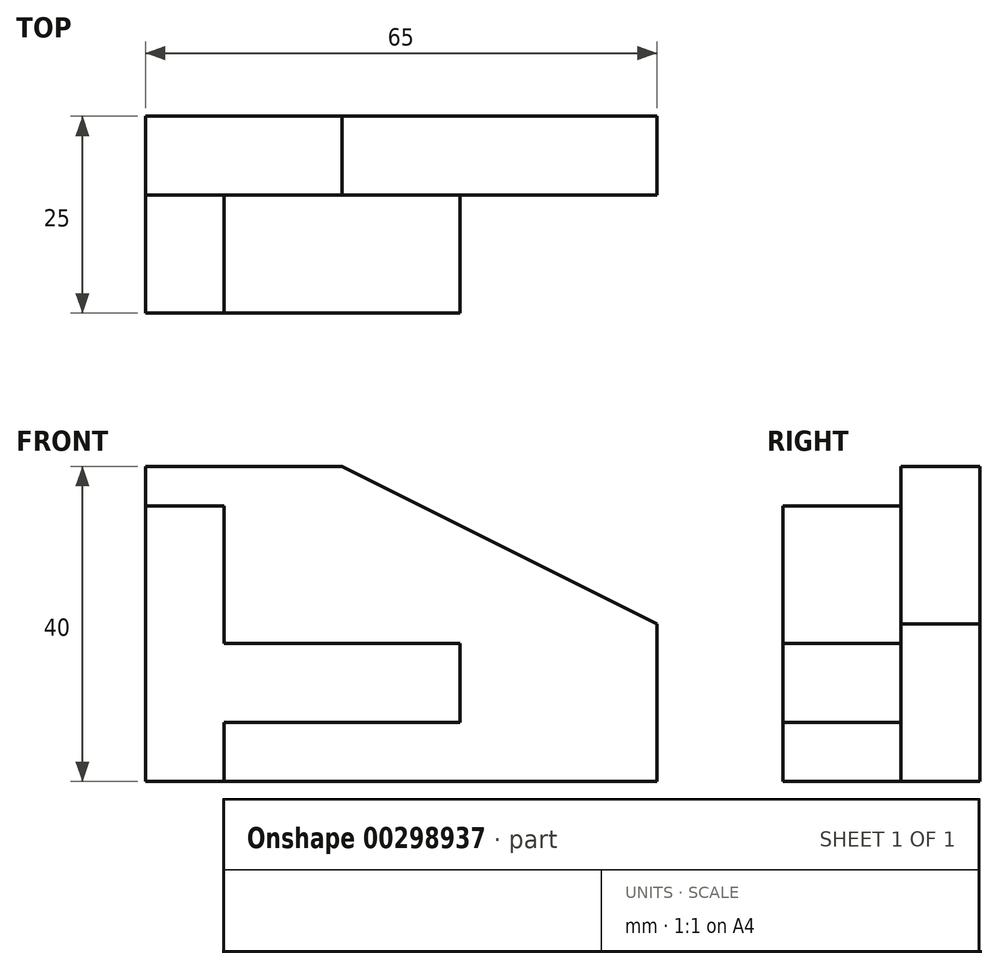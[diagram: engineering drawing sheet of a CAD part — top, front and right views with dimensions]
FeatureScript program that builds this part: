
annotation { "Feature Type Name" : "Feature", "Feature Type Description" : "" }
export const myFeature = defineFeature(function(context is Context, id is Id, definition is map)
    precondition{}
    {
        {
            var Q0;
            Q0=qCreatedBy(makeId("Front.planeOp"),FACE);
            var sketch = newSketch(context, id + "F0", { "sketchPlane" : qUnion([Q0])});
            skLineSegment(sketch, "E0.bottom", {"start": v(-74.93, 35.29) * mm, "end": v(-64.93, 35.29) * mm});
            skLineSegment(sketch, "E0.top", {"start": v(-74.93, 0.29) * mm, "end": v(-64.93, 0.29) * mm});
            skLineSegment(sketch, "E0.left", {"start": v(-74.93, 35.29) * mm, "end": v(-74.93, 0.29) * mm});
            skLineSegment(sketch, "E0.right", {"start": v(-64.93, 35.29) * mm, "end": v(-64.93, 0.29) * mm});
            skLineSegment(sketch, "E1.bottom", {"start": v(-74.93, 0.29) * mm, "end": v(-9.93, 0.29) * mm});
            skLineSegment(sketch, "E1.left", {"start": v(-74.93, 0.29) * mm, "end": v(-74.93, 40.29) * mm});
            skLineSegment(sketch, "E2", {"start": v(-9.93, 0.29) * mm, "end": v(-9.93, 20.29) * mm});
            skLineSegment(sketch, "E3", {"start": v(-74.93, 40.29) * mm, "end": v(-49.93, 40.29) * mm});
            skLineSegment(sketch, "E4", {"start": v(-49.93, 40.29) * mm, "end": v(-9.93, 20.29) * mm});
            skLineSegment(sketch, "E5.bottom", {"start": v(-64.93, 17.79) * mm, "end": v(-34.93, 17.79) * mm});
            skLineSegment(sketch, "E5.top", {"start": v(-64.93, 7.79) * mm, "end": v(-34.93, 7.79) * mm});
            skLineSegment(sketch, "E5.left", {"start": v(-64.93, 17.79) * mm, "end": v(-64.93, 7.79) * mm});
            skLineSegment(sketch, "E5.right", {"start": v(-34.93, 17.79) * mm, "end": v(-34.93, 7.79) * mm});
            skSolve(sketch);
        }
        {
            var Q0;
            Q0=makeQuery(id+"F0.imprint","IMPRINT",FACE,{"disambiguationData":[TD([[makeQuery(id+"F0.imprint","IMPRINT",EDGE,{"derivedFrom":sQuery(id+"F0.wireOp",EDGE,"E0.bottom")}),-1.0]])]});
            extrude(context, id + "F1", {"entities" : qUnion([Q0]), "depth" : 25 * mm});
        }
        {
            var Q0;
            {var subQ4=sQuery(id+"F0.wireOp",EDGE,"E0.bottom");Q0=makeQuery(id+"F0.imprint","IMPRINT",FACE,{"disambiguationData":[TD([[makeQuery(id+"F0.imprint","IMPRINT",EDGE,{"derivedFrom":subQ4}),1.0]])]});}
            extrude(context, id + "F2", {"entities" : qUnion([Q0]), "operationType" : NewBodyOperationType.ADD, "depth" : 10 * mm});
        }
        {
            var Q0;
            Q0=makeQuery(id+"F0.imprint","IMPRINT",FACE,{"disambiguationData":[TD([[makeQuery(id+"F0.imprint","IMPRINT",EDGE,{"derivedFrom":sQuery(id+"F0.wireOp",EDGE,"E5.bottom")}),-1.0]])]});
            extrude(context, id + "F3", {"entities" : qUnion([Q0]), "operationType" : NewBodyOperationType.ADD, "depth" : 25 * mm});
        }
    });
